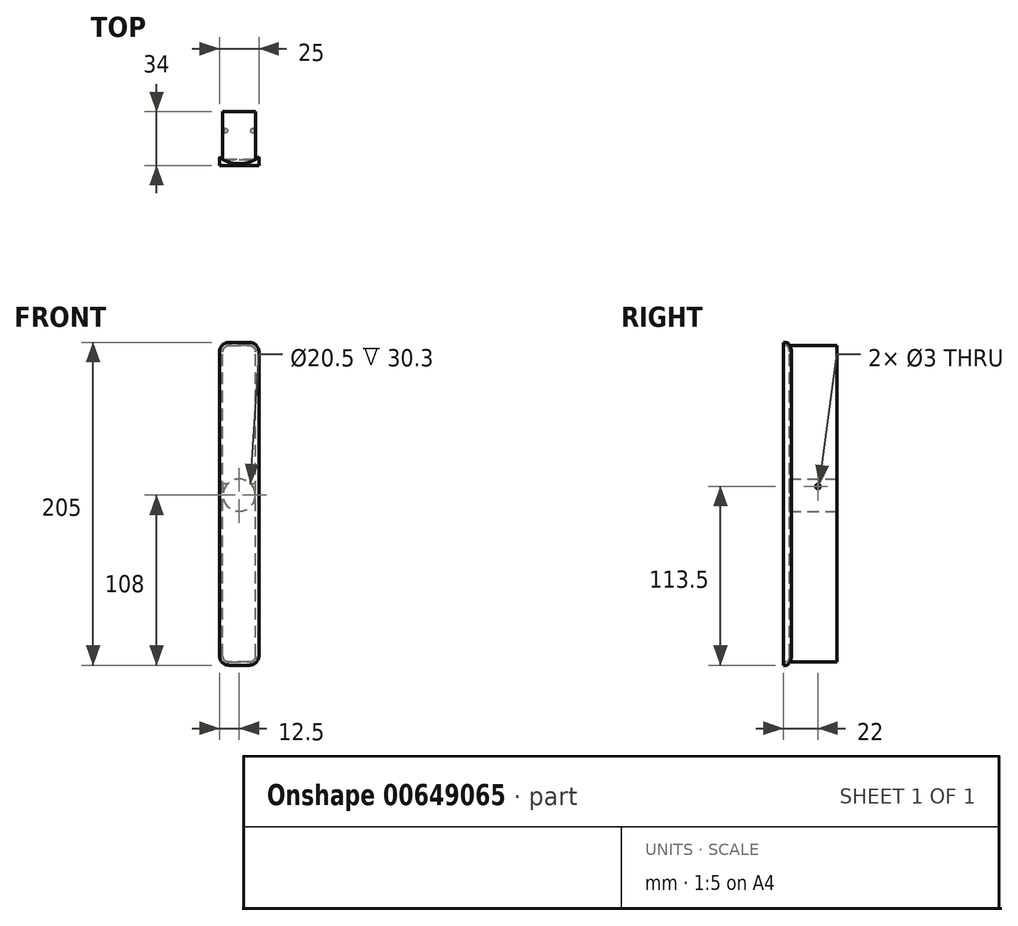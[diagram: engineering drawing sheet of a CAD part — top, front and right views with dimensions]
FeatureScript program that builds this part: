
annotation { "Feature Type Name" : "Feature", "Feature Type Description" : "" }
export const myFeature = defineFeature(function(context is Context, id is Id, definition is map)
    precondition{}
    {
        {
            var Q0;
            Q0=qCreatedBy(makeId("Front.planeOp"),FACE);
            var sketch = newSketch(context, id + "F0", { "sketchPlane" : qUnion([Q0])});
            skLineSegment(sketch, "E0.bottom", {"start": v(6.5, -100.5) * mm, "end": v(-6.5, -100.5) * mm});
            skLineSegment(sketch, "E0.top", {"start": v(6.5, 100.5) * mm, "end": v(-6.5, 100.5) * mm});
            skLineSegment(sketch, "E0.left", {"start": v(10.5, -96.5) * mm, "end": v(10.5, 96.5) * mm});
            skLineSegment(sketch, "E0.right", {"start": v(-10.5, -96.5) * mm, "end": v(-10.5, 96.5) * mm});
            skPoint(sketch, "E0.middle", {"position": v(0, 0) * mm});
            skPoint(sketch, "E1.visualSharp", {"position": v(-10.5, 100.5) * mm});
            skArc(sketch, "E1.filletArc", {"start": v(-6.5, 100.5) * mm, "mid": v(-9.33, 99.33) * mm, "end": v(-10.5, 96.5) * mm});
            skPoint(sketch, "E2.visualSharp", {"position": v(10.5, 100.5) * mm});
            skArc(sketch, "E2.filletArc", {"start": v(10.5, 96.5) * mm, "mid": v(9.33, 99.33) * mm, "end": v(6.5, 100.5) * mm});
            skPoint(sketch, "E3.visualSharp", {"position": v(10.5, -100.5) * mm});
            skArc(sketch, "E3.filletArc", {"start": v(6.5, -100.5) * mm, "mid": v(9.33, -99.33) * mm, "end": v(10.5, -96.5) * mm});
            skPoint(sketch, "E4.visualSharp", {"position": v(-10.5, -100.5) * mm});
            skArc(sketch, "E4.filletArc", {"start": v(-10.5, -96.5) * mm, "mid": v(-9.33, -99.33) * mm, "end": v(-6.5, -100.5) * mm});
            skSolve(sketch);
        }
        {
            var Q0;
            Q0=qCreatedBy(makeId("Front.planeOp"),FACE);
            var sketch = newSketch(context, id + "F1", { "sketchPlane" : qUnion([Q0])});
            skLineSegment(sketch, "E5.0", {"start": v(12.5, -96.5) * mm, "end": v(12.5, 96.5) * mm});
            skArc(sketch, "E5.1", {"start": v(6.5, -102.5) * mm, "mid": v(10.74, -100.74) * mm, "end": v(12.5, -96.5) * mm});
            skArc(sketch, "E5.2", {"start": v(12.5, 96.5) * mm, "mid": v(10.74, 100.74) * mm, "end": v(6.5, 102.5) * mm});
            skLineSegment(sketch, "E5.3", {"start": v(-6.5, -102.5) * mm, "end": v(6.5, -102.5) * mm});
            skLineSegment(sketch, "E5.4", {"start": v(6.5, 102.5) * mm, "end": v(-6.5, 102.5) * mm});
            skArc(sketch, "E5.5", {"start": v(-6.5, 102.5) * mm, "mid": v(-10.74, 100.74) * mm, "end": v(-12.5, 96.5) * mm});
            skLineSegment(sketch, "E5.6", {"start": v(-12.5, 96.5) * mm, "end": v(-12.5, -96.5) * mm});
            skArc(sketch, "E5.7", {"start": v(-12.5, -96.5) * mm, "mid": v(-10.74, -100.74) * mm, "end": v(-6.5, -102.5) * mm});
            skSolve(sketch);
        }
        {
            var Q0;
            Q0=makeQuery(id+"F1.imprint","IMPRINT",FACE,{"disambiguationData":[TD([[makeQuery(id+"F1.imprint","IMPRINT",EDGE,{"derivedFrom":sQuery(id+"F1.wireOp",EDGE,"E5.0")}),1.0]])]});
            extrude(context, id + "F2", {"entities" : qUnion([Q0]), "depth" : 6 * mm, "offsetDistance" : 25 * mm});
        }
        {
            var Q0;
            Q0=qCreatedBy(makeId("Top.planeOp"),FACE);
            var sketch = newSketch(context, id + "F3", { "sketchPlane" : qUnion([Q0])});
            skCircle(sketch, "E6", {"center": v(0, 16) * mm, "radius": 21 * mm});
            skSolve(sketch);
        }
        {
            var Q0;
            Q0=makeQuery(id+"F3.imprint","IMPRINT",FACE,{"disambiguationData":[TD([[makeQuery(id+"F3.imprint","IMPRINT",EDGE,{"derivedFrom":sQuery(id+"F3.wireOp",EDGE,"E6")}),1.0]])]});
            var Q1;
            Q1=sQuery(id+"F3.wireOp",EDGE,"E6");
            extrude(context, id + "F4", {"entities" : qUnion([Q0]), "operationType" : NewBodyOperationType.REMOVE, "surfaceEntities" : qUnion([Q1]), "endBound" : BoundingType.THROUGH_ALL, "oppositeDirection" : true, "depth" : 25 * mm, "offsetDistance" : 25 * mm, "hasSecondDirection" : true, "secondDirectionBound" : SecondDirectionBoundingType.THROUGH_ALL, "secondDirectionOppositeDirection" : false, "secondDirectionDepth" : 25 * mm});
        }
        {
            var Q0;
            Q0=makeQuery(id+"F0.imprint","IMPRINT",FACE,{"disambiguationData":[TD([[makeQuery(id+"F0.imprint","IMPRINT",EDGE,{"derivedFrom":sQuery(id+"F0.wireOp",EDGE,"E0.bottom")}),-1.0]])]});
            extrude(context, id + "F5", {"entities" : qUnion([Q0]), "operationType" : NewBodyOperationType.ADD, "oppositeDirection" : true, "depth" : 28 * mm, "offsetDistance" : 25 * mm, "hasSecondDirection" : true, "secondDirectionBound" : SecondDirectionBoundingType.UP_TO_NEXT, "secondDirectionOppositeDirection" : false, "secondDirectionDepth" : 25 * mm});
        }
        {
            var Q0;
            Q0=makeQuery(id+"F5.opExtrude","CAP_FACE",FACE,{"disambiguationData":[OSD([sQuery(id+"F0.wireOp",EDGE,"E0.bottom"),sQuery(id+"F0.wireOp",EDGE,"E0.top"),sQuery(id+"F0.wireOp",EDGE,"E0.left"),sQuery(id+"F0.wireOp",EDGE,"E0.right"),sQuery(id+"F0.wireOp",EDGE,"E1.filletArc"),sQuery(id+"F0.wireOp",EDGE,"E2.filletArc"),sQuery(id+"F0.wireOp",EDGE,"E3.filletArc"),sQuery(id+"F0.wireOp",EDGE,"E4.filletArc")])],"isStart":false});
            var sketch = newSketch(context, id + "F6", { "sketchPlane" : qUnion([Q0])});
            skCircle(sketch, "E7", {"center": v(0, 5.5) * mm, "radius": 10.25 * mm});
            skSolve(sketch);
        }
        {
            var Q0;
            Q0=makeQuery(id+"F6.imprint","IMPRINT",FACE,{"disambiguationData":[TD([[makeQuery(id+"F6.imprint","IMPRINT",EDGE,{"derivedFrom":sQuery(id+"F6.wireOp",EDGE,"E7")}),1.0]])]});
            extrude(context, id + "F7", {"entities" : qUnion([Q0]), "operationType" : NewBodyOperationType.REMOVE, "oppositeDirection" : true, "depth" : 30.3 * mm, "offsetDistance" : 25 * mm});
        }
        {
            var Q0;
            Q0=makeQuery(id+"F5.opExtrude","SWEPT_FACE",FACE,{"disambiguationData":[OSD([sQuery(id+"F0.wireOp",EDGE,"E0.right")])]});
            var sketch = newSketch(context, id + "F8", { "sketchPlane" : qUnion([Q0])});
            skPoint(sketch, "E8", {"position": v(-16, 11) * mm});
            skSolve(sketch);
        }
        {
            var Q0;
            Q0=sQuery(id+"F8.wireOp",VERTEX,"E8");
            var Q1;
            Q1=makeQuery(id+"F2.opExtrude","SWEPT_BODY",BODY,{"disambiguationData":[OSD([sQuery(id+"F1.wireOp",EDGE,"E5.0"),sQuery(id+"F1.wireOp",EDGE,"E5.1"),sQuery(id+"F1.wireOp",EDGE,"E5.2"),sQuery(id+"F1.wireOp",EDGE,"E5.3"),sQuery(id+"F1.wireOp",EDGE,"E5.4"),sQuery(id+"F1.wireOp",EDGE,"E5.5"),sQuery(id+"F1.wireOp",EDGE,"E5.6"),sQuery(id+"F1.wireOp",EDGE,"E5.7")])]});
            hole(context, id + "F9", {"style" : HoleStyle.SIMPLE, "endStyle" : HoleEndStyle.THROUGH, "holeDiameter" : 3 * mm, "majorDiameter" : 5 * mm, "isTappedThrough" : true, "tappedDepth" : 12 * mm, "tapClearance" : 3, "locations" : qUnion([Q0]), "scope" : qUnion([Q1])});
        }
    });
